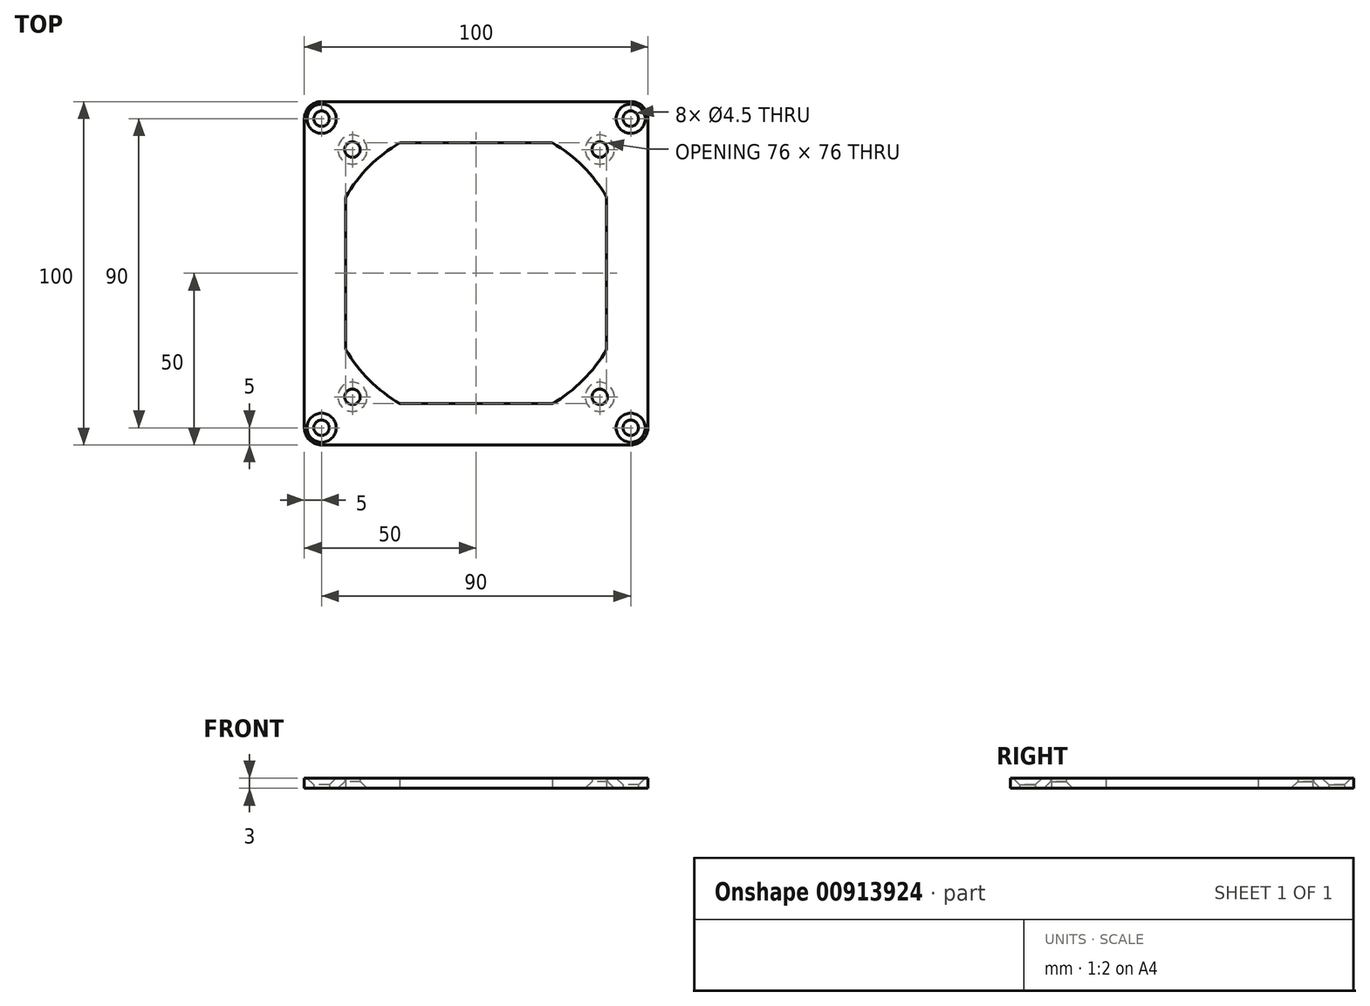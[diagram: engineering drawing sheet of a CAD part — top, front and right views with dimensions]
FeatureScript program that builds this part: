
annotation { "Feature Type Name" : "Feature", "Feature Type Description" : "" }
export const myFeature = defineFeature(function(context is Context, id is Id, definition is map)
    precondition{}
    {
        {
            var Q0;
            Q0=qCreatedBy(makeId("Top.planeOp"),FACE);
            var sketch = newSketch(context, id + "F0", { "sketchPlane" : qUnion([Q0])});
            skLineSegment(sketch, "E0.bottom", {"start": v(0, 0) * mm, "end": v(100, 0) * mm});
            skLineSegment(sketch, "E0.top", {"start": v(0, 100) * mm, "end": v(100, 100) * mm});
            skLineSegment(sketch, "E0.left", {"start": v(0, 0) * mm, "end": v(0, 100) * mm});
            skLineSegment(sketch, "E0.right", {"start": v(100, 0) * mm, "end": v(100, 100) * mm});
            skLineSegment(sketch, "E1", {"start": v(50, 0) * mm, "end": v(50, 117.06) * mm, "construction": true});
            skLineSegment(sketch, "E2", {"start": v(0, 50) * mm, "end": v(162.6, 50) * mm, "construction": true});
            skLineSegment(sketch, "E3.bottom", {"start": v(27.82, 12) * mm, "end": v(72.18, 12) * mm});
            skLineSegment(sketch, "E3.top", {"start": v(27.82, 88) * mm, "end": v(72.18, 88) * mm});
            skLineSegment(sketch, "E3.left", {"start": v(12, 27.82) * mm, "end": v(12, 72.18) * mm});
            skLineSegment(sketch, "E3.right", {"start": v(88, 27.82) * mm, "end": v(88, 72.18) * mm});
            skPoint(sketch, "E3.middle", {"position": v(50, 50) * mm});
            skArc(sketch, "E4", {"start": v(27.82, 88) * mm, "mid": v(18.89, 81.11) * mm, "end": v(12, 72.18) * mm});
            skPoint(sketch, "E5.orphan", {"position": v(12, 88) * mm});
            skPoint(sketch, "E6.orphan", {"position": v(88, 88) * mm});
            skArc(sketch, "E7.trimOffspring", {"start": v(88, 72.18) * mm, "mid": v(81.11, 81.11) * mm, "end": v(72.18, 88) * mm});
            skPoint(sketch, "E8.orphan", {"position": v(88, 12) * mm});
            skArc(sketch, "E9.trimOffspring", {"start": v(72.18, 12) * mm, "mid": v(81.11, 18.89) * mm, "end": v(88, 27.82) * mm});
            skPoint(sketch, "E10.orphan", {"position": v(12, 12) * mm});
            skArc(sketch, "E11.trimOffspring", {"start": v(12, 27.82) * mm, "mid": v(18.89, 18.89) * mm, "end": v(27.82, 12) * mm});
            skCircle(sketch, "E12", {"center": v(14, 86) * mm, "radius": 2.25 * mm});
            skCircle(sketch, "E13.MirrorC", {"center": v(86, 86) * mm, "radius": 2.25 * mm});
            skCircle(sketch, "E14.MirrorC", {"center": v(14, 14) * mm, "radius": 2.25 * mm});
            skCircle(sketch, "E15.MirrorC", {"center": v(86, 14) * mm, "radius": 2.25 * mm});
            skCircle(sketch, "E16", {"center": v(5, 95) * mm, "radius": 2.25 * mm});
            skCircle(sketch, "E17.MirrorC", {"center": v(95, 95) * mm, "radius": 2.25 * mm});
            skLineSegment(sketch, "E18.MirrorCS", {"start": v(100, 50) * mm, "end": v(-62.6, 50) * mm, "construction": true});
            skCircle(sketch, "E19.MirrorC", {"center": v(95, 5) * mm, "radius": 2.25 * mm});
            skCircle(sketch, "E20.MirrorC", {"center": v(5, 5) * mm, "radius": 2.25 * mm});
            skSolve(sketch);
        }
        {
            var Q0;
            Q0=makeQuery(id+"F0.imprint","IMPRINT",FACE,{"disambiguationData":[TD([[makeQuery(id+"F0.imprint","IMPRINT",EDGE,{"derivedFrom":sQuery(id+"F0.wireOp",EDGE,"E0.bottom")}),1.0]])]});
            extrude(context, id + "F1", {"entities" : qUnion([Q0]), "depth" : 3 * mm, "offsetDistance" : 25 * mm});
        }
        {
            var Q0;
            Q0=makeQuery(id+"F1.opExtrude","SWEPT_EDGE",EDGE,{"disambiguationData":[OSD([sQuery(id+"F0.wireOp",EDGE,"E0.bottom"),sQuery(id+"F0.wireOp",EDGE,"E0.right")])]});
            var Q1;
            Q1=makeQuery(id+"F1.opExtrude","SWEPT_EDGE",EDGE,{"disambiguationData":[OSD([sQuery(id+"F0.wireOp",EDGE,"E0.top"),sQuery(id+"F0.wireOp",EDGE,"E0.right")])]});
            var Q2;
            Q2=makeQuery(id+"F1.opExtrude","SWEPT_EDGE",EDGE,{"disambiguationData":[OSD([sQuery(id+"F0.wireOp",EDGE,"E0.bottom"),sQuery(id+"F0.wireOp",EDGE,"E0.left")])]});
            var Q3;
            Q3=makeQuery(id+"F1.opExtrude","SWEPT_EDGE",EDGE,{"disambiguationData":[OSD([sQuery(id+"F0.wireOp",EDGE,"E0.top"),sQuery(id+"F0.wireOp",EDGE,"E0.left")])]});
            fillet(context, id + "F2", {"entities" : qUnion([Q0, Q1, Q2, Q3]), "radius" : 5 * mm, "tangentPropagation" : true, "allowEdgeOverflow" : false});
        }
        {
            var Q0;
            Q0=makeQuery(id+"F1.opExtrude","CAP_EDGE",EDGE,{"disambiguationData":[OSD([sQuery(id+"F0.wireOp",EDGE,"E16")])],"isStart":false});
            var Q1;
            Q1=makeQuery(id+"F1.opExtrude","CAP_EDGE",EDGE,{"disambiguationData":[OSD([sQuery(id+"F0.wireOp",EDGE,"E20.MirrorC")])],"isStart":false});
            var Q2;
            Q2=makeQuery(id+"F1.opExtrude","CAP_EDGE",EDGE,{"disambiguationData":[OSD([sQuery(id+"F0.wireOp",EDGE,"E19.MirrorC")])],"isStart":false});
            var Q3;
            Q3=makeQuery(id+"F1.opExtrude","CAP_EDGE",EDGE,{"disambiguationData":[OSD([sQuery(id+"F0.wireOp",EDGE,"E17.MirrorC")])],"isStart":false});
            var Q4;
            Q4=makeQuery(id+"F1.opExtrude","CAP_EDGE",EDGE,{"disambiguationData":[OSD([sQuery(id+"F0.wireOp",EDGE,"E12")])],"isStart":true});
            var Q5;
            Q5=makeQuery(id+"F1.opExtrude","CAP_EDGE",EDGE,{"disambiguationData":[OSD([sQuery(id+"F0.wireOp",EDGE,"E14.MirrorC")])],"isStart":true});
            var Q6;
            Q6=makeQuery(id+"F1.opExtrude","CAP_EDGE",EDGE,{"disambiguationData":[OSD([sQuery(id+"F0.wireOp",EDGE,"E15.MirrorC")])],"isStart":true});
            var Q7;
            Q7=makeQuery(id+"F1.opExtrude","CAP_EDGE",EDGE,{"disambiguationData":[OSD([sQuery(id+"F0.wireOp",EDGE,"E13.MirrorC")])],"isStart":true});
            chamfer(context, id + "F3", {"entities" : qUnion([Q0, Q1, Q2, Q3, Q4, Q5, Q6, Q7]), "width" : 2 * mm, "tangentPropagation" : true});
        }
    });
